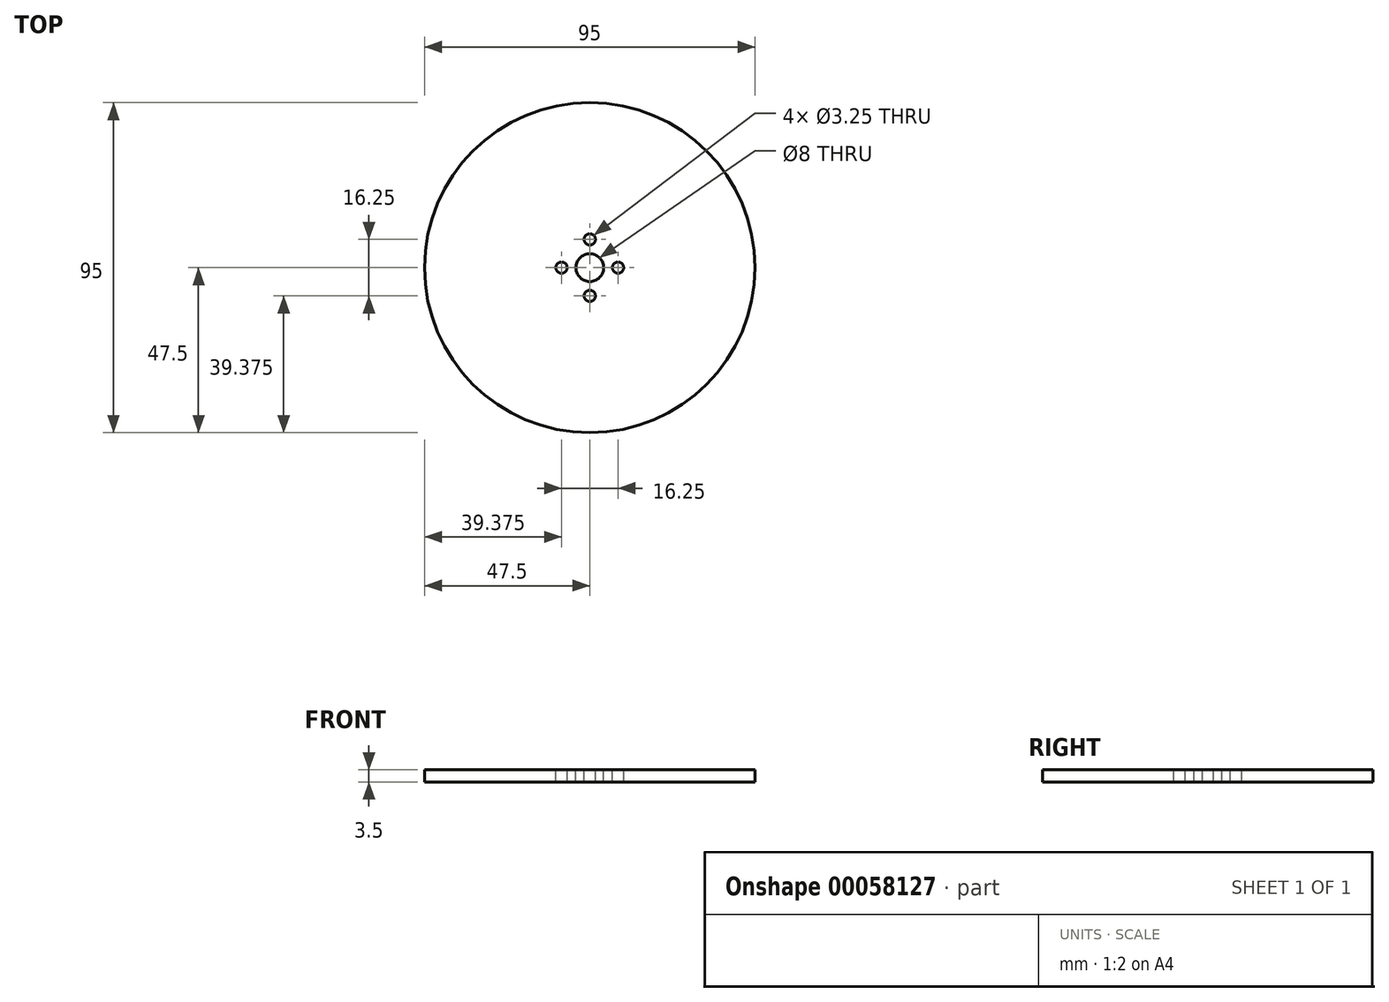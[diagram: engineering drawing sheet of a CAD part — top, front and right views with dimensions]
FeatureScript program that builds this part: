
annotation { "Feature Type Name" : "Feature", "Feature Type Description" : "" }
export const myFeature = defineFeature(function(context is Context, id is Id, definition is map)
    precondition{}
    {
        {
            var Q0;
            Q0=qCreatedBy(makeId("Top.planeOp"),FACE);
            var sketch = newSketch(context, id + "F0", { "sketchPlane" : qUnion([Q0])});
            skCircle(sketch, "E0", {"center": v(0, 0) * mm, "radius": 47.5 * mm});
            skSolve(sketch);
        }
        {
            var Q0;
            Q0=makeQuery(id+"F0.imprint","IMPRINT",FACE,{"disambiguationData":[TD([[makeQuery(id+"F0.imprint","IMPRINT",EDGE,{"derivedFrom":sQuery(id+"F0.wireOp",EDGE,"E0")}),1.0]])]});
            extrude(context, id + "F1", {"entities" : qUnion([Q0]), "depth" : 3.5 * mm});
        }
        {
            var Q0;
            Q0=makeQuery(id+"F1.opExtrude","CAP_FACE",FACE,{"disambiguationData":[OSD([sQuery(id+"F0.wireOp",EDGE,"E0")])],"isStart":false});
            var sketch = newSketch(context, id + "F2", { "sketchPlane" : qUnion([Q0])});
            skCircle(sketch, "E1", {"center": v(0, 0) * mm, "radius": 4 * mm});
            skSolve(sketch);
        }
        {
            var Q0;
            Q0=makeQuery(id+"F2.imprint","IMPRINT",FACE,{"disambiguationData":[TD([[makeQuery(id+"F2.imprint","IMPRINT",EDGE,{"derivedFrom":sQuery(id+"F2.wireOp",EDGE,"E1")}),1.0]])]});
            extrude(context, id + "F3", {"entities" : qUnion([Q0]), "operationType" : NewBodyOperationType.REMOVE, "oppositeDirection" : true, "depth" : 3.5 * mm});
        }
        {
            var Q0;
            Q0=makeQuery(id+"F1.opExtrude","CAP_FACE",FACE,{"disambiguationData":[OSD([sQuery(id+"F0.wireOp",EDGE,"E0")])],"isStart":false});
            var sketch = newSketch(context, id + "F4", { "sketchPlane" : qUnion([Q0])});
            skCircle(sketch, "E2", {"center": v(0, 8.12) * mm, "radius": 1.63 * mm});
            skCircle(sketch, "E3.1.0", {"center": v(-8.12, 0) * mm, "radius": 1.63 * mm});
            skCircle(sketch, "E3.2.0", {"center": v(0, -8.12) * mm, "radius": 1.63 * mm});
            skCircle(sketch, "E3.3.0", {"center": v(8.12, 0) * mm, "radius": 1.63 * mm});
            skPoint(sketch, "E3.center", {"position": v(0, 0) * mm});
            skSolve(sketch);
        }
        {
            var Q0;
            Q0=makeQuery(id+"F4.imprint","IMPRINT",FACE,{"disambiguationData":[TD([[makeQuery(id+"F4.imprint","IMPRINT",EDGE,{"derivedFrom":sQuery(id+"F4.wireOp",EDGE,"E2")}),1.0]])]});
            var Q1;
            Q1=makeQuery(id+"F4.imprint","IMPRINT",FACE,{"disambiguationData":[TD([[makeQuery(id+"F4.imprint","IMPRINT",EDGE,{"derivedFrom":sQuery(id+"F4.wireOp",EDGE,"E3.1.0")}),1.0]])]});
            var Q2;
            Q2=makeQuery(id+"F4.imprint","IMPRINT",FACE,{"disambiguationData":[TD([[makeQuery(id+"F4.imprint","IMPRINT",EDGE,{"derivedFrom":sQuery(id+"F4.wireOp",EDGE,"E3.2.0")}),1.0]])]});
            var Q3;
            Q3=makeQuery(id+"F4.imprint","IMPRINT",FACE,{"disambiguationData":[TD([[makeQuery(id+"F4.imprint","IMPRINT",EDGE,{"derivedFrom":sQuery(id+"F4.wireOp",EDGE,"E3.3.0")}),1.0]])]});
            extrude(context, id + "F5", {"entities" : qUnion([Q0, Q1, Q2, Q3]), "operationType" : NewBodyOperationType.REMOVE, "oppositeDirection" : true, "depth" : 3.5 * mm});
        }
    });
